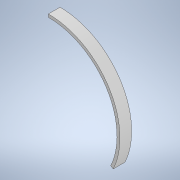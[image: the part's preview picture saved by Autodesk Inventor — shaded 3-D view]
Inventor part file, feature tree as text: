
AUTODESK INVENTOR PART (.ipt)
format: ipt  version: 2021 (Build 250183000, 183)  size: 102,400 bytes
history: native  units: in
note: dims shown in document units (in); Inventor stores cm internally (conversion verified against a paired STEP export)
features: extrude x1, sketch x1
ambient origin geometry x8: Origin, YZ Plane, XZ Plane, XY Plane, X Axis, Y Axis, Z Axis, Center Point
bodies: Solid1 (feature_tree)
feature tree (2):
  extrude  "Extrusion1"  Depth=1.0in
  sketch  "Sketch1"  dims[d0=11.75in d1=12.25in d2=120.0deg d3=1.0in d4=0.0in]
